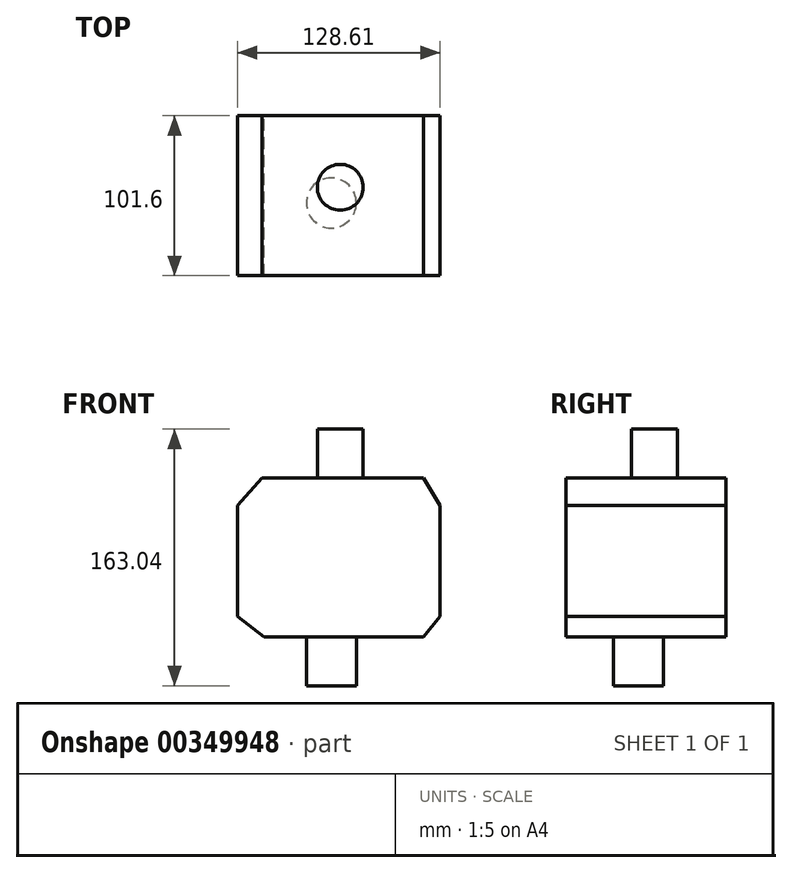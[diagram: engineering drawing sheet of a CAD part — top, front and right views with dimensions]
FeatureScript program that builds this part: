
annotation { "Feature Type Name" : "Feature", "Feature Type Description" : "" }
export const myFeature = defineFeature(function(context is Context, id is Id, definition is map)
    precondition{}
    {
        {
            var Q0;
            Q0=qCreatedBy(makeId("Front.planeOp"),FACE);
            var sketch = newSketch(context, id + "F0", { "sketchPlane" : qUnion([Q0])});
            skLineSegment(sketch, "E0", {"start": v(-43.92, 47.22) * mm, "end": v(-59.56, 29.78) * mm});
            skLineSegment(sketch, "E1", {"start": v(-59.56, 29.78) * mm, "end": v(-59.56, -40.6) * mm});
            skLineSegment(sketch, "E2", {"start": v(-59.56, -40.6) * mm, "end": v(-42.71, -53.84) * mm});
            skLineSegment(sketch, "E3", {"start": v(-42.71, -53.84) * mm, "end": v(58.65, -53.84) * mm});
            skLineSegment(sketch, "E4", {"start": v(58.65, -53.84) * mm, "end": v(69.05, -40.6) * mm});
            skLineSegment(sketch, "E5", {"start": v(69.05, -40.6) * mm, "end": v(69.05, 29.78) * mm});
            skLineSegment(sketch, "E6", {"start": v(69.05, 29.78) * mm, "end": v(58.65, 47.22) * mm});
            skLineSegment(sketch, "E7", {"start": v(58.65, 47.22) * mm, "end": v(-43.92, 47.22) * mm});
            skSolve(sketch);
        }
        {
            var Q0;
            Q0 = qSketchRegion(id + "F0", true);
            extrude(context, id + "F1", {"entities" : qUnion([Q0]), "depth" : 101.6 * mm, "offsetDistance" : 25.4 * mm});
        }
        {
            var Q0;
            Q0=makeQuery(id+"F1.opExtrude","SWEPT_FACE",FACE,{"disambiguationData":[OSD([sQuery(id+"F0.wireOp",EDGE,"E7")])]});
            var sketch = newSketch(context, id + "F2", { "sketchPlane" : qUnion([Q0])});
            skCircle(sketch, "E8", {"center": v(5.68, -45.48) * mm, "radius": 14.57 * mm});
            skSolve(sketch);
        }
        {
            var Q0;
            Q0 = qSketchRegion(id + "F2", true);
            extrude(context, id + "F3", {"entities" : qUnion([Q0]), "operationType" : NewBodyOperationType.ADD, "depth" : 30.99 * mm, "offsetDistance" : 25.4 * mm});
        }
        {
            var Q0;
            Q0=makeQuery(id+"F1.opExtrude","SWEPT_FACE",FACE,{"disambiguationData":[OSD([sQuery(id+"F0.wireOp",EDGE,"E3")])]});
            var sketch = newSketch(context, id + "F4", { "sketchPlane" : qUnion([Q0])});
            skCircle(sketch, "E9", {"center": v(0, 55.45) * mm, "radius": 15.89 * mm});
            skSolve(sketch);
        }
        {
            var Q0;
            Q0 = qSketchRegion(id + "F4", true);
            extrude(context, id + "F5", {"entities" : qUnion([Q0]), "operationType" : NewBodyOperationType.ADD, "depth" : 30.99 * mm, "offsetDistance" : 25.4 * mm});
        }
    });
